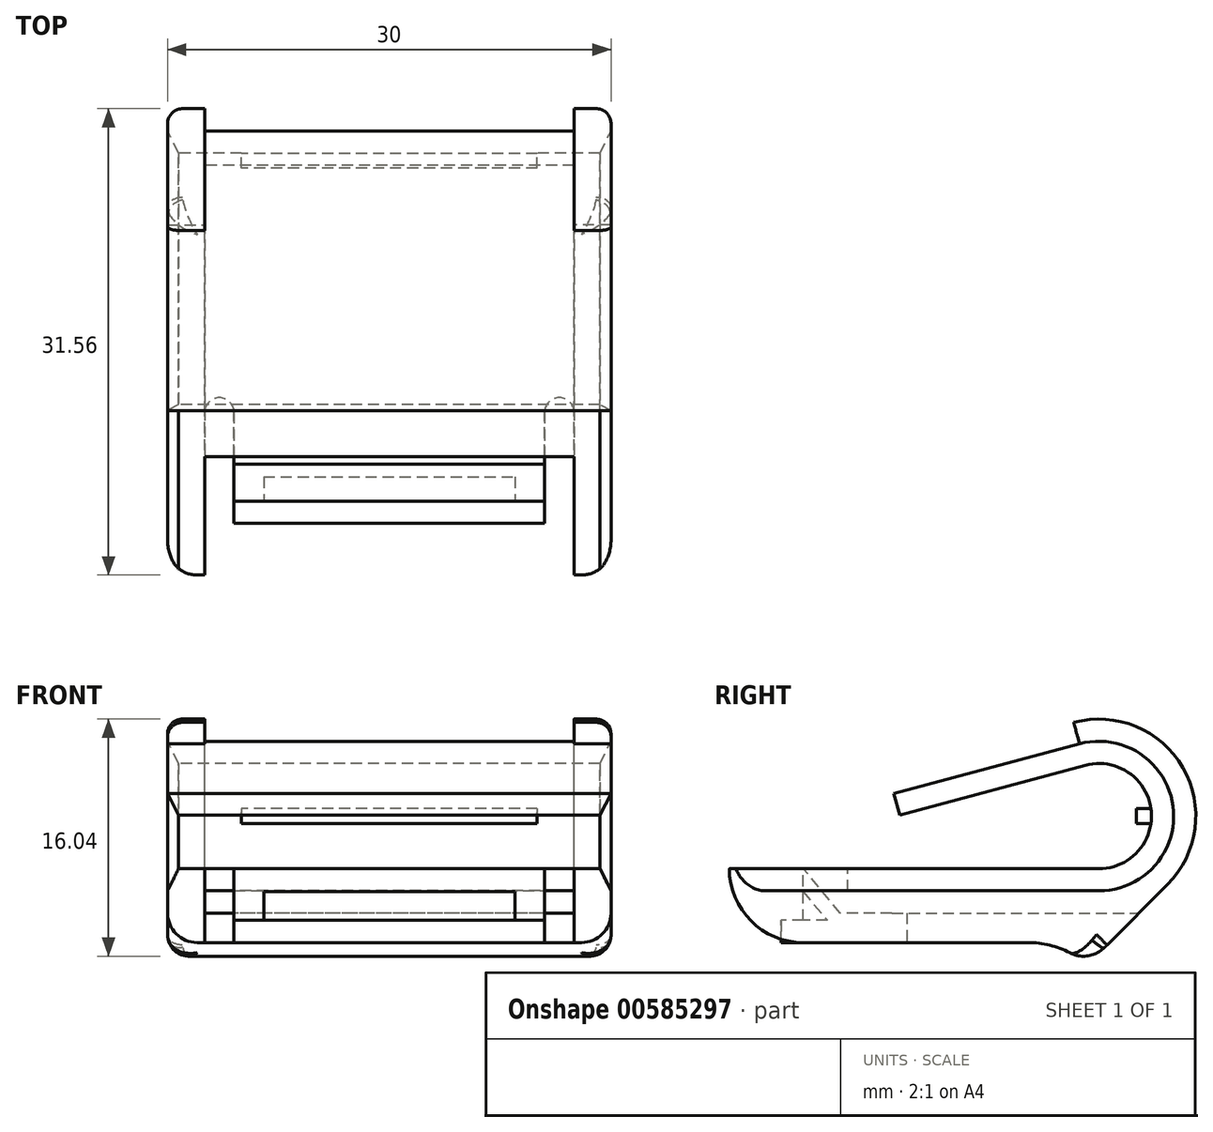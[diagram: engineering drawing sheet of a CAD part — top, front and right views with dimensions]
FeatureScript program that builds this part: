
annotation { "Feature Type Name" : "Feature", "Feature Type Description" : "" }
export const myFeature = defineFeature(function(context is Context, id is Id, definition is map)
    precondition{}
    {
        {
            var Q0;
            Q0=qCreatedBy(makeId("Right.planeOp"),FACE);
            var sketch = newSketch(context, id + "F0", { "sketchPlane" : qUnion([Q0])});
            skLineSegment(sketch, "E0", {"start": v(0, 0) * mm, "end": v(25, 0) * mm});
            skArc(sketch, "E1", {"start": v(25, 0) * mm, "mid": v(28.53, 4.03) * mm, "end": v(24.08, 7) * mm});
            skLineSegment(sketch, "E2", {"start": v(24.08, 7) * mm, "end": v(11.52, 3.64) * mm});
            skLineSegment(sketch, "E3", {"start": v(11.52, 3.64) * mm, "end": v(10.74, 6.53) * mm});
            skLineSegment(sketch, "E4", {"start": v(10.74, 6.53) * mm, "end": v(23.3, 9.9) * mm});
            skLineSegment(sketch, "E5", {"start": v(23.3, 9.9) * mm, "end": v(23.7, 8.45) * mm});
            skLineSegment(sketch, "E6", {"start": v(23.7, 8.45) * mm, "end": v(11.13, 5.08) * mm});
            skArc(sketch, "E7", {"start": v(29.64, -1.08) * mm, "mid": v(30.68, 6.84) * mm, "end": v(23.3, 9.9) * mm});
            skLineSegment(sketch, "E8", {"start": v(29.64, -1.08) * mm, "end": v(24.22, -6.5) * mm});
            skArc(sketch, "E9", {"start": v(24.22, -6.5) * mm, "mid": v(22.35, -5.39) * mm, "end": v(20.22, -5) * mm});
            skLineSegment(sketch, "E10", {"start": v(20.22, -5) * mm, "end": v(5, -5) * mm});
            skArc(sketch, "E11", {"start": v(0, 0) * mm, "mid": v(1.46, -3.54) * mm, "end": v(5, -5) * mm});
            skLineSegment(sketch, "E12.bottom", {"start": v(27.53, 4.06) * mm, "end": v(28.53, 4.06) * mm});
            skLineSegment(sketch, "E12.top", {"start": v(27.53, 3.06) * mm, "end": v(28.53, 3.06) * mm});
            skLineSegment(sketch, "E12.left", {"start": v(27.53, 4.06) * mm, "end": v(27.53, 3.06) * mm});
            skPoint(sketch, "E12.middle", {"position": v(28.56, 3.56) * mm});
            skArc(sketch, "E13", {"start": v(25, -1.5) * mm, "mid": v(30.02, 4.22) * mm, "end": v(23.7, 8.45) * mm});
            skLineSegment(sketch, "E14", {"start": v(25, -1.5) * mm, "end": v(7, -1.5) * mm});
            skLineSegment(sketch, "E15", {"start": v(7, -1.5) * mm, "end": v(7, 0) * mm});
            skLineSegment(sketch, "E16", {"start": v(5, 0) * mm, "end": v(7.52, -3) * mm});
            skLineSegment(sketch, "E17", {"start": v(7.52, -3) * mm, "end": v(27.72, -3) * mm});
            skLineSegment(sketch, "E18", {"start": v(5, 0) * mm, "end": v(5, -5) * mm});
            skSolve(sketch);
        }
        {
            var Q0;
            {var subQ3=sQuery(id+"F0.wireOp",EDGE,"E0");Q0=makeQuery(id+"F0.imprint","IMPRINT",FACE,{"disambiguationData":[TD([[makeQuery(id+"F0.imprint","IMPRINT",EDGE,{"derivedFrom":subQ3}),-1.0]])]});}
            var Q1;
            {var subQ0=sQuery(id+"F0.wireOp",EDGE,"E9");Q1=makeQuery(id+"F0.imprint","IMPRINT",FACE,{"disambiguationData":[TD([[makeQuery(id+"F0.imprint","IMPRINT",EDGE,{"derivedFrom":subQ0}),-1.0]])]});}
            var Q2;
            Q2=makeQuery(id+"F0.imprint","IMPRINT",FACE,{"disambiguationData":[TD([[makeQuery(id+"F0.imprint","IMPRINT",EDGE,{"derivedFrom":sQuery(id+"F0.wireOp",EDGE,"E5")}),1.0]])]});
            var Q3;
            {var subQ0=sQuery(id+"F0.wireOp",EDGE,"E2");Q3=makeQuery(id+"F0.imprint","IMPRINT",FACE,{"disambiguationData":[TD([[makeQuery(id+"F0.imprint","IMPRINT",EDGE,{"derivedFrom":subQ0}),-1.0]])]});}
            extrude(context, id + "F1", {"entities" : qUnion([Q0, Q1, Q2, Q3]), "depth" : 15 * mm, "offsetDistance" : 25 * mm});
        }
        {
            var Q0;
            Q0=makeQuery(id+"F0.imprint","IMPRINT",FACE,{"disambiguationData":[TD([[makeQuery(id+"F0.imprint","IMPRINT",EDGE,{"derivedFrom":sQuery(id+"F0.wireOp",EDGE,"E5")}),1.0]])]});
            extrude(context, id + "F2", {"entities" : qUnion([Q0]), "operationType" : NewBodyOperationType.REMOVE, "depth" : 12.5 * mm, "offsetDistance" : 25 * mm});
        }
        {
            var Q0;
            {var subQ0=sQuery(id+"F0.wireOp",EDGE,"E11");Q0=makeQuery(id+"F0.imprint","IMPRINT",FACE,{"disambiguationData":[TD([[makeQuery(id+"F0.imprint","IMPRINT",EDGE,{"derivedFrom":subQ0}),1.0]])]});}
            extrude(context, id + "F3", {"entities" : qUnion([Q0]), "operationType" : NewBodyOperationType.REMOVE, "depth" : 12.5 * mm, "offsetDistance" : 25 * mm});
        }
        {
            var Q0;
            Q0=makeQuery(id+"F1.opExtrude","SWEPT_FACE",FACE,{"disambiguationData":[OSD([sQuery(id+"F0.wireOp",EDGE,"E0")])]});
            var sketch = newSketch(context, id + "F4", { "sketchPlane" : qUnion([Q0])});
            skLineSegment(sketch, "E19.bottom", {"start": v(0, 7) * mm, "end": v(10.5, 7) * mm});
            skLineSegment(sketch, "E19.top", {"start": v(0, 8) * mm, "end": v(12.5, 8) * mm});
            skLineSegment(sketch, "E19.left", {"start": v(0, 7) * mm, "end": v(0, 8) * mm});
            skLineSegment(sketch, "E19.right", {"start": v(12.5, 7) * mm, "end": v(12.5, 8) * mm});
            skLineSegment(sketch, "E20.top", {"start": v(12.5, 0) * mm, "end": v(10.5, 0) * mm});
            skLineSegment(sketch, "E20.left", {"start": v(12.5, 7) * mm, "end": v(12.5, 0) * mm});
            skLineSegment(sketch, "E20.right", {"start": v(10.5, 7) * mm, "end": v(10.5, 0) * mm});
            skSolve(sketch);
        }
        {
            var Q0;
            Q0 = qSketchRegion(id + "F4", true);
            var Q1;
            Q1=makeQuery(id+"F2.boolean.opBoolean","COPY",FACE,{"derivedFrom":makeQuery(id+"F2.opExtrude","SWEPT_FACE",FACE,{"disambiguationData":[OSD([sQuery(id+"F0.wireOp",EDGE,"E14")])]})});
            extrude(context, id + "F5", {"entities" : qUnion([Q0]), "operationType" : NewBodyOperationType.REMOVE, "endBound" : BoundingType.UP_TO_SURFACE, "oppositeDirection" : true, "depth" : 25 * mm, "endBoundEntityFace" : qUnion([Q1]), "offsetDistance" : 25 * mm});
        }
        {
            var Q0;
            Q0=makeQuery(id+"F1.opExtrude","SWEPT_FACE",FACE,{"disambiguationData":[OSD([sQuery(id+"F0.wireOp",EDGE,"E10")])]});
            var sketch = newSketch(context, id + "F6", { "sketchPlane" : qUnion([Q0])});
            skLineSegment(sketch, "E21.bottom", {"start": v(12.5, -5) * mm, "end": v(10.5, -5) * mm});
            skLineSegment(sketch, "E21.top", {"start": v(11.5, -12) * mm, "end": v(11.5, -12) * mm});
            skLineSegment(sketch, "E21.left", {"start": v(12.5, -5) * mm, "end": v(12.5, -11) * mm});
            skLineSegment(sketch, "E21.right", {"start": v(10.5, -5) * mm, "end": v(10.5, -11) * mm});
            skPoint(sketch, "E22.visualSharp", {"position": v(10.5, -12) * mm});
            skArc(sketch, "E22.filletArc", {"start": v(10.5, -11) * mm, "mid": v(10.8, -11.7) * mm, "end": v(11.5, -12) * mm});
            skPoint(sketch, "E23.visualSharp", {"position": v(12.5, -12) * mm});
            skArc(sketch, "E23.filletArc", {"start": v(11.5, -12) * mm, "mid": v(12.2, -11.7) * mm, "end": v(12.5, -11) * mm});
            skSolve(sketch);
        }
        {
            var Q0;
            Q0 = qSketchRegion(id + "F6", true);
            var Q1;
            Q1=makeQuery(id+"F2.boolean.opBoolean","COPY",FACE,{"derivedFrom":makeQuery(id+"F2.opExtrude","SWEPT_FACE",FACE,{"disambiguationData":[OSD([sQuery(id+"F0.wireOp",EDGE,"E14")])]})});
            extrude(context, id + "F7", {"entities" : qUnion([Q0]), "operationType" : NewBodyOperationType.REMOVE, "endBound" : BoundingType.UP_TO_SURFACE, "oppositeDirection" : true, "depth" : 25 * mm, "endBoundEntityFace" : qUnion([Q1]), "offsetDistance" : 25 * mm});
        }
        {
            var Q0;
            Q0=makeQuery(id+"F1.opExtrude","SWEPT_BODY",BODY,{"disambiguationData":[OSD([sQuery(id+"F0.wireOp",EDGE,"E0"),sQuery(id+"F0.wireOp",EDGE,"E1"),sQuery(id+"F0.wireOp",EDGE,"E2"),sQuery(id+"F0.wireOp",EDGE,"E3"),sQuery(id+"F0.wireOp",EDGE,"E5"),sQuery(id+"F0.wireOp",EDGE,"E6"),sQuery(id+"F0.wireOp",EDGE,"E7"),sQuery(id+"F0.wireOp",EDGE,"E8"),sQuery(id+"F0.wireOp",EDGE,"E9"),sQuery(id+"F0.wireOp",EDGE,"E10"),sQuery(id+"F0.wireOp",EDGE,"E11")])]});
            var Q1;
            {var subQ0=sQuery(id+"F0.wireOp",EDGE,"E10");var subQ1=sQuery(id+"F0.wireOp",EDGE,"E0");var subQ2=sQuery(id+"F0.wireOp",EDGE,"E8");var subQ3=sQuery(id+"F0.wireOp",EDGE,"E9");var subQ4=sQuery(id+"F0.wireOp",EDGE,"E11");Q1=makeQuery(id+"F2.boolean.opBoolean","SPLIT",FACE,{"disambiguationData":[TD([makeQuery(id+"F1.opExtrude","SWEPT_FACE",FACE,{"disambiguationData":[OSD([subQ2])]})])],"derivedFrom":makeQuery(id+"F1.opExtrude","CAP_FACE",FACE,{"disambiguationData":[OSD([subQ1,sQuery(id+"F0.wireOp",EDGE,"E1"),sQuery(id+"F0.wireOp",EDGE,"E2"),sQuery(id+"F0.wireOp",EDGE,"E3"),sQuery(id+"F0.wireOp",EDGE,"E5"),sQuery(id+"F0.wireOp",EDGE,"E6"),sQuery(id+"F0.wireOp",EDGE,"E7"),subQ2,subQ3,subQ0,subQ4])],"isStart":true})});}
            mirror(context, id + "F8", {"operationType" : NewBodyOperationType.ADD, "entities" : qUnion([Q0]), "mirrorPlane" : qUnion([Q1])});
        }
        {
            var Q0;
            Q0=makeQuery(id+"F8.opPattern","COPY",EDGE,{"derivedFrom":makeQuery(id+"F1.opExtrude","CAP_EDGE",EDGE,{"disambiguationData":[OSD([sQuery(id+"F0.wireOp",EDGE,"E0")])],"isStart":false}),"instanceName":"1"});
            var Q1;
            Q1=makeQuery(id+"F1.opExtrude","CAP_EDGE",EDGE,{"disambiguationData":[OSD([sQuery(id+"F0.wireOp",EDGE,"E0")])],"isStart":false});
            chamfer(context, id + "F9", {"entities" : qUnion([Q0, Q1]), "chamferType" : ChamferType.TWO_OFFSETS, "width1" : 1.5 * mm, "oppositeDirection" : false, "width2" : .75 * mm, "tangentPropagation" : true});
        }
        {
            var Q0;
            Q0=makeQuery(id+"F1.opExtrude","CAP_EDGE",EDGE,{"disambiguationData":[OSD([sQuery(id+"F0.wireOp",EDGE,"E11")])],"isStart":false});
            var Q1;
            Q1=makeQuery(id+"F8.opPattern","COPY",EDGE,{"derivedFrom":makeQuery(id+"F1.opExtrude","CAP_EDGE",EDGE,{"disambiguationData":[OSD([sQuery(id+"F0.wireOp",EDGE,"E11")])],"isStart":false}),"instanceName":"1"});
            var Q2;
            {var subQ0=makeQuery(id+"F1.opExtrude","SWEPT_EDGE",EDGE,{"disambiguationData":[OSD([sQuery(id+"F0.wireOp",EDGE,"E8"),sQuery(id+"F0.wireOp",EDGE,"E9")])]});Q2=makeQuery(id+"F8.boolean.opBoolean","MERGE",EDGE,{"derivedFrom":[subQ0,makeQuery(id+"F8.opPattern","COPY",EDGE,{"derivedFrom":subQ0,"instanceName":"1"})]});}
            fillet(context, id + "F10", {"entities" : qUnion([Q0, Q1, Q2]), "radius" : 2 * mm, "tangentPropagation" : true, "allowEdgeOverflow" : false});
        }
        {
            var Q0;
            {var subQ0=sQuery(id+"F0.wireOp",EDGE,"E9");var subQ1=makeQuery(id+"F1.opExtrude","SWEPT_EDGE",EDGE,{"disambiguationData":[OSD([sQuery(id+"F0.wireOp",EDGE,"E8"),subQ0])]});Q0=makeQuery(id+"F10.opFillet","BLEND_EDGE",EDGE,{"blendedFrom":[makeQuery(id+"F1.opExtrude","CAP_EDGE",EDGE,{"disambiguationData":[OSD([subQ0])],"isStart":false}),makeQuery(id+"F8.boolean.opBoolean","MERGE",EDGE,{"derivedFrom":[subQ1,makeQuery(id+"F8.opPattern","COPY",EDGE,{"derivedFrom":subQ1,"instanceName":"1"})]})],"blendedInto":[]});}
            var Q1;
            {var subQ0=sQuery(id+"F0.wireOp",EDGE,"E9");var subQ1=makeQuery(id+"F1.opExtrude","SWEPT_EDGE",EDGE,{"disambiguationData":[OSD([sQuery(id+"F0.wireOp",EDGE,"E8"),subQ0])]});Q1=makeQuery(id+"F10.opFillet","BLEND_EDGE",EDGE,{"blendedFrom":[makeQuery(id+"F8.opPattern","COPY",EDGE,{"derivedFrom":makeQuery(id+"F1.opExtrude","CAP_EDGE",EDGE,{"disambiguationData":[OSD([subQ0])],"isStart":false}),"instanceName":"1"}),makeQuery(id+"F8.boolean.opBoolean","MERGE",EDGE,{"derivedFrom":[subQ1,makeQuery(id+"F8.opPattern","COPY",EDGE,{"derivedFrom":subQ1,"instanceName":"1"})]})],"blendedInto":[]});}
            fillet(context, id + "F11", {"entities" : qUnion([Q0, Q1]), "radius" : 1 * mm, "tangentPropagation" : true, "allowEdgeOverflow" : false});
        }
        {
            var Q0;
            {var subQ0=sQuery(id+"F0.wireOp",EDGE,"E12.bottom");Q0=makeQuery(id+"F0.imprint","IMPRINT",FACE,{"disambiguationData":[TD([[makeQuery(id+"F0.imprint","IMPRINT",EDGE,{"derivedFrom":subQ0}),-1.0]])]});}
            extrude(context, id + "F12", {"entities" : qUnion([Q0]), "operationType" : NewBodyOperationType.ADD, "endBound" : BoundingType.SYMMETRIC, "depth" : 20 * mm, "offsetDistance" : 25 * mm});
        }
        {
            var Q0;
            Q0=qCreatedBy(makeId("Right.planeOp"),FACE);
            var sketch = newSketch(context, id + "F13", { "sketchPlane" : qUnion([Q0])});
            skLineSegment(sketch, "E24", {"start": v(5, -1.56) * mm, "end": v(6.63, -3.5) * mm});
            skLineSegment(sketch, "E25", {"start": v(6.63, -3.5) * mm, "end": v(5, -3.5) * mm});
            skLineSegment(sketch, "E26", {"start": v(5, -3.5) * mm, "end": v(5, -1.56) * mm});
            skLineSegment(sketch, "E27.bottom", {"start": v(5, -3.5) * mm, "end": v(3.5, -3.5) * mm});
            skLineSegment(sketch, "E27.top", {"start": v(5, -5) * mm, "end": v(3.5, -5) * mm});
            skLineSegment(sketch, "E27.left", {"start": v(5, -3.5) * mm, "end": v(5, -5) * mm});
            skLineSegment(sketch, "E27.right", {"start": v(3.5, -3.5) * mm, "end": v(3.5, -5) * mm});
            skSolve(sketch);
        }
        {
            var Q0;
            Q0=makeQuery(id+"F13.imprint","IMPRINT",FACE,{"disambiguationData":[TD([[makeQuery(id+"F13.imprint","IMPRINT",EDGE,{"derivedFrom":sQuery(id+"F13.wireOp",EDGE,"E27.bottom")}),1.0]])]});
            var Q1;
            Q1=makeQuery(id+"F8.opPattern","COPY",FACE,{"derivedFrom":makeQuery(id+"F7.boolean.opBoolean","MERGE",FACE,{"derivedFrom":[makeQuery(id+"F5.boolean.opBoolean","COPY",FACE,{"derivedFrom":makeQuery(id+"F5.opExtrude","SWEPT_FACE",FACE,{"disambiguationData":[OSD([sQuery(id+"F4.wireOp",EDGE,"E20.right")])]})}),makeQuery(id+"F7.opExtrude","SWEPT_FACE",FACE,{"disambiguationData":[OSD([sQuery(id+"F6.wireOp",EDGE,"E21.right")])]})]}),"instanceName":"1"});
            var Q2;
            Q2=makeQuery(id+"F7.boolean.opBoolean","MERGE",FACE,{"derivedFrom":[makeQuery(id+"F5.boolean.opBoolean","COPY",FACE,{"derivedFrom":makeQuery(id+"F5.opExtrude","SWEPT_FACE",FACE,{"disambiguationData":[OSD([sQuery(id+"F4.wireOp",EDGE,"E20.right")])]})}),makeQuery(id+"F7.opExtrude","SWEPT_FACE",FACE,{"disambiguationData":[OSD([sQuery(id+"F6.wireOp",EDGE,"E21.right")])]})]});
            extrude(context, id + "F14", {"entities" : qUnion([Q0]), "operationType" : NewBodyOperationType.ADD, "endBound" : BoundingType.UP_TO_SURFACE, "oppositeDirection" : true, "depth" : 20 * mm, "endBoundEntityFace" : qUnion([Q1]), "offsetDistance" : 25 * mm, "hasSecondDirection" : true, "secondDirectionBound" : SecondDirectionBoundingType.UP_TO_SURFACE, "secondDirectionOppositeDirection" : false, "secondDirectionDepth" : 25 * mm, "secondDirectionBoundEntityFace" : qUnion([Q2])});
        }
        {
            var Q0;
            Q0=makeQuery(id+"F13.imprint","IMPRINT",FACE,{"disambiguationData":[TD([[makeQuery(id+"F13.imprint","IMPRINT",EDGE,{"derivedFrom":sQuery(id+"F13.wireOp",EDGE,"E24")}),-1.0]])]});
            extrude(context, id + "F15", {"entities" : qUnion([Q0]), "operationType" : NewBodyOperationType.REMOVE, "endBound" : BoundingType.SYMMETRIC, "oppositeDirection" : true, "depth" : 17 * mm, "offsetDistance" : 25 * mm});
        }
    });
